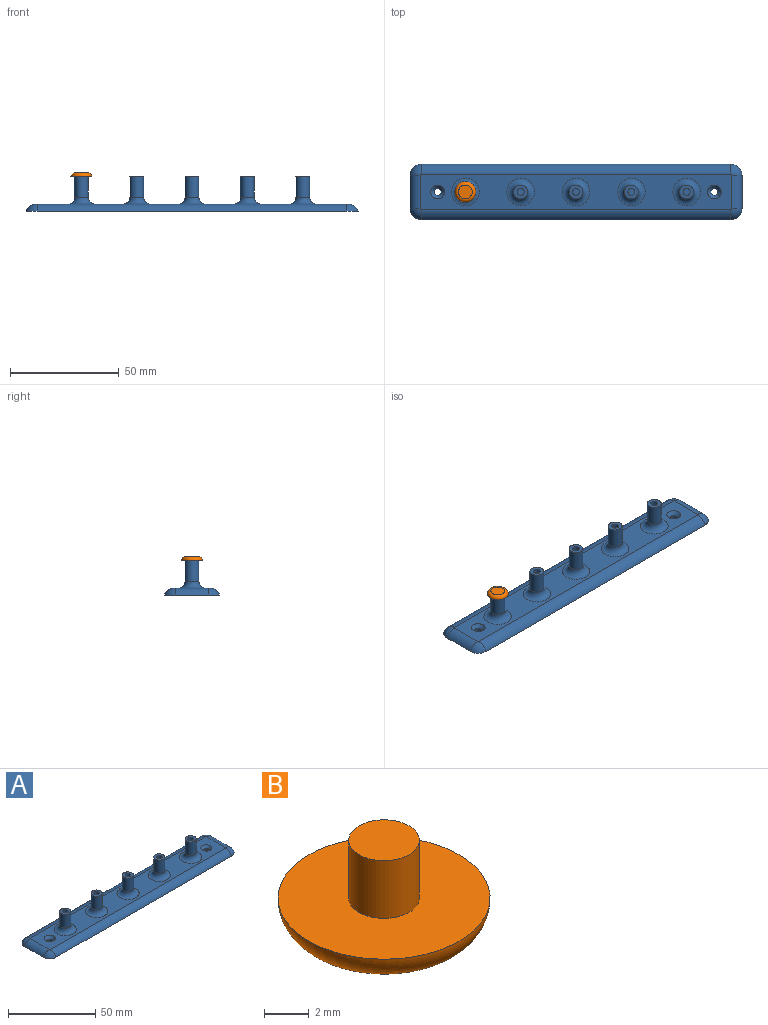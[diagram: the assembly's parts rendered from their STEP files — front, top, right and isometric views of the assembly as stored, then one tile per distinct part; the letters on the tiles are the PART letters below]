
ASSEMBLY  parts=2 mates=1
PART A: 39 faces, bbox 152.4x25.4x15.9 mm
  f0: plane 142.98x15.98mm, normal (0,0,1), area 1588.2mm2, adj f13,f15,f26,f27,f28,f29,f30,f31
  f1: plane 152.4x25.4mm, normal (0,0,-1), area 3833mm2, adj f12,f14,f26,f27,f28,f29,f30,f31
  f2: cylinder r=3.17mm len=9.53mm, axis (0,0,-1), area 190mm2, adj f3,f34
  f3: plane 6.35x6.35mm, normal (0,0,1), area 23.8mm2, adj f2,f16
  f4: cylinder r=3.17mm len=9.53mm, axis (0,0,-1), area 190mm2, adj f5,f38
  f5: plane 6.35x6.35mm, normal (0,0,1), area 23.8mm2, adj f4,f18
  f6: cylinder r=3.17mm len=9.53mm, axis (0,0,-1), area 190mm2, adj f7,f37
  f7: plane 6.35x6.35mm, normal (0,0,1), area 23.8mm2, adj f6,f20
  f8: cylinder r=3.17mm len=9.53mm, axis (0,0,-1), area 190mm2, adj f9,f36
  f9: plane 6.35x6.35mm, normal (0,0,1), area 23.8mm2, adj f8,f22
  f10: cylinder r=3.17mm len=9.53mm, axis (0,0,-1), area 190mm2, adj f11,f35
  f11: plane 6.35x6.35mm, normal (0,0,1), area 23.8mm2, adj f10,f24
  f12: cylinder r=1.59mm len=3.18mm, axis (0,0,1), area 15.8mm2, adj f1,f13
  f13: cone r=1.59mm half-angle=45deg, axis (0,0,1), area 33.6mm2, adj f0,f12
  f14: cylinder r=1.59mm len=3.18mm, axis (0,0,1), area 15.8mm2, adj f1,f15
  f15: cone r=1.59mm half-angle=45deg, axis (0,0,1), area 33.6mm2, adj f0,f14
  f16: cylinder r=1.59mm len=6.35mm, axis (0,0,1), area 63.3mm2, adj f3,f17
  f17: plane 3.18x3.18mm, normal (0,0,1), area 7.9mm2, adj f16
  f18: cylinder r=1.59mm len=12.7mm, axis (0,0,1), area 126.7mm2, adj f5,f19
  f19: plane 3.18x3.18mm, normal (0,0,1), area 7.9mm2, adj f18
  f20: cylinder r=1.59mm len=12.7mm, axis (0,0,1), area 126.7mm2, adj f7,f21
  f21: plane 3.18x3.18mm, normal (0,0,1), area 7.9mm2, adj f20
  f22: cylinder r=1.59mm len=12.7mm, axis (0,0,1), area 126.7mm2, adj f9,f23
  f23: plane 3.18x3.18mm, normal (0,0,1), area 7.9mm2, adj f22
  f24: cylinder r=1.59mm len=12.7mm, axis (0,0,1), area 126.7mm2, adj f11,f25
  f25: plane 3.18x3.18mm, normal (0,0,1), area 7.9mm2, adj f24
  f26: cylinder r=5.08mm len=142.24mm, axis (-1,0,0), area 857.3mm2, adj f0,f1,f27,f28
  f27: torus R=0.37mm, axis (0,0,-1), area 28.8mm2, adj f0,f1,f26,f29
  f28: torus R=0.37mm, axis (0,0,-1), area 28.8mm2, adj f0,f1,f26,f30
  f29: cylinder r=5.08mm len=15.24mm, axis (0,1,0), area 91.9mm2, adj f0,f1,f27,f31
  f30: cylinder r=5.08mm len=15.24mm, axis (0,1,0), area 91.9mm2, adj f0,f1,f28,f32
  f31: torus R=0.37mm, axis (0,0,-1), area 28.8mm2, adj f0,f1,f29,f33
  f32: torus R=0.37mm, axis (0,0,-1), area 28.8mm2, adj f0,f1,f30,f33
  f33: cylinder r=5.08mm len=142.24mm, axis (-1,0,0), area 857.3mm2, adj f0,f1,f31,f32
  f34: torus R=6.35mm, axis (0,0,1), area 135.6mm2, adj f0,f2
  f35: torus R=6.35mm, axis (0,0,1), area 135.6mm2, adj f0,f10
  f36: torus R=6.35mm, axis (0,0,1), area 135.6mm2, adj f0,f8
  f37: torus R=6.35mm, axis (0,0,1), area 135.6mm2, adj f0,f6
  f38: torus R=6.35mm, axis (0,0,1), area 135.6mm2, adj f0,f4
PART B: 5 faces, bbox 10.3x10.3x4.8 mm
  f0: plane 9.53x9.53mm, normal (0,0,1), area 63.3mm2, adj f2,f4
  f1: plane 6.35x6.35mm, normal (0,0,-1), area 31.7mm2, adj f4
  f2: cylinder r=1.59mm len=3.18mm, axis (0,0,-1), area 31.7mm2, adj f0,f3
  f3: plane 3.18x3.18mm, normal (0,0,1), area 7.9mm2, adj f2
  f4: torus R=3.17mm, axis (0,0,1), area 65.6mm2, adj f0,f1
PLACE A rot(axis=(1,0,0),0deg) t=(4.11,-28.58,-12.25)mm
PLACE B rot(axis=(-1,0,0),180deg) t=(-46.69,-28.58,5.21)mm
MATE revolute A.f16 <-> B.f2  axis (0,0,1) through (-46.69,-28.58,3.63)mm
